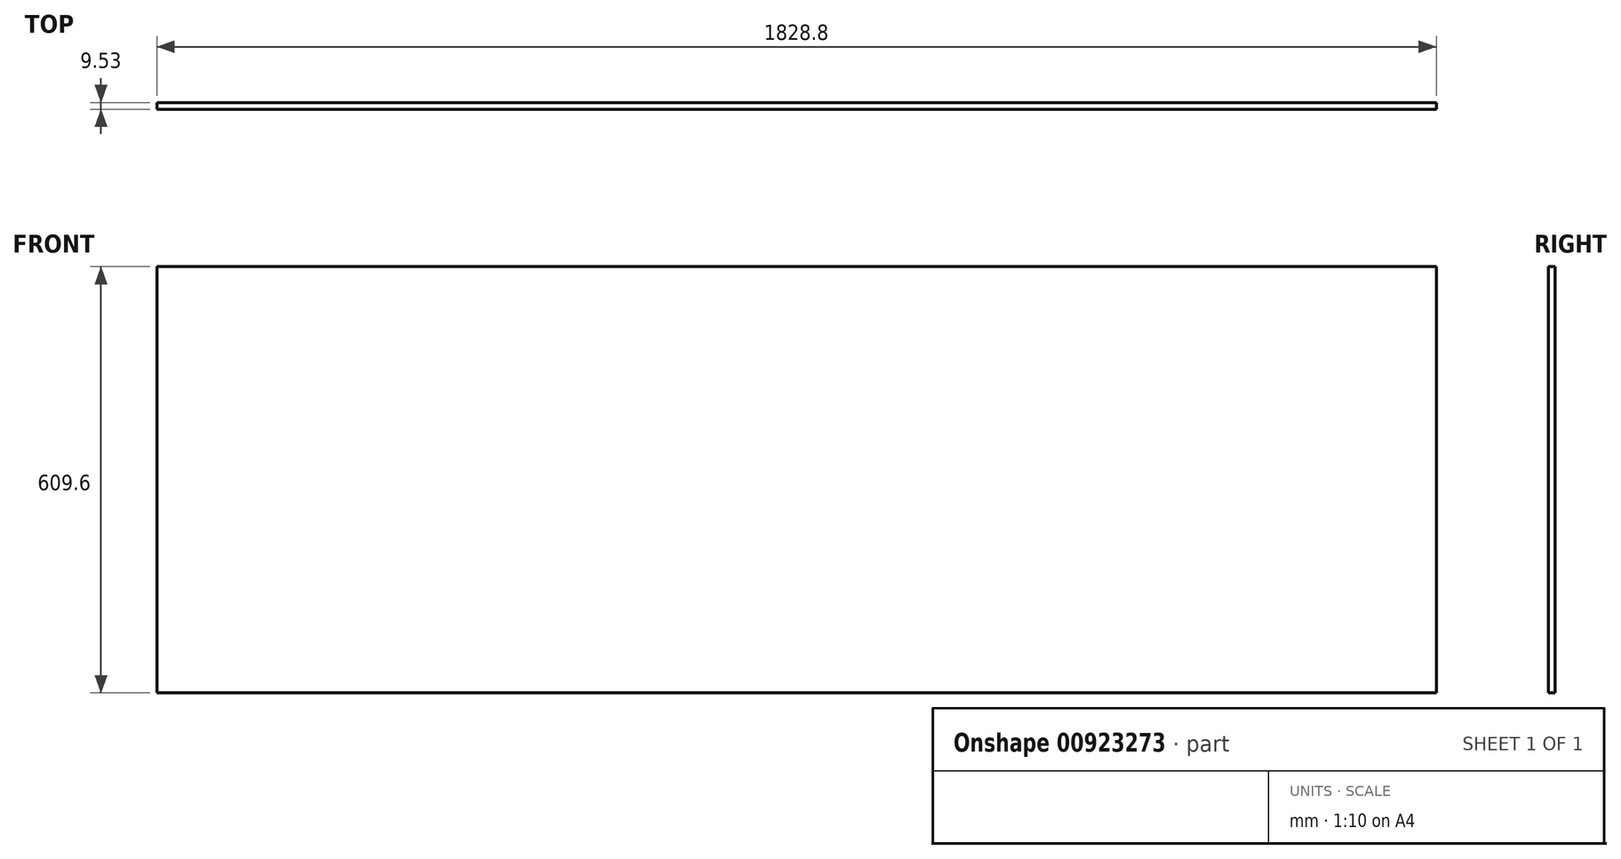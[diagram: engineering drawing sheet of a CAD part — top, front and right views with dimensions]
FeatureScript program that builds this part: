
annotation { "Feature Type Name" : "Feature", "Feature Type Description" : "" }
export const myFeature = defineFeature(function(context is Context, id is Id, definition is map)
    precondition{}
    {
        {
            var Q0;
            Q0=qCreatedBy(makeId("Front.planeOp"),FACE);
            var sketch = newSketch(context, id + "F0", { "sketchPlane" : qUnion([Q0])});
            skLineSegment(sketch, "E0.bottom", {"start": v(0, 0) * mm, "end": v(1828.8, 0) * mm});
            skLineSegment(sketch, "E0.top", {"start": v(0, 609.6) * mm, "end": v(1828.8, 609.6) * mm});
            skLineSegment(sketch, "E0.left", {"start": v(0, 0) * mm, "end": v(0, 609.6) * mm});
            skLineSegment(sketch, "E0.right", {"start": v(1828.8, 0) * mm, "end": v(1828.8, 609.6) * mm});
            skPoint(sketch, "E1", {"position": v(0, 609.6) * mm});
            skPoint(sketch, "E2", {"position": v(44.45, 609.6) * mm});
            skPoint(sketch, "E3", {"position": v(44.45, 533.4) * mm});
            skPoint(sketch, "E4", {"position": v(1784.35, 609.6) * mm});
            skPoint(sketch, "E5", {"position": v(1784.35, 533.4) * mm});
            skSolve(sketch);
        }
        {
            var Q0;
            Q0=makeQuery(id+"F0.imprint","IMPRINT",FACE,{"disambiguationData":[TD([[makeQuery(id+"F0.imprint","IMPRINT",EDGE,{"derivedFrom":sQuery(id+"F0.wireOp",EDGE,"E0.bottom")}),1.0]])]});
            extrude(context, id + "F1", {"entities" : qUnion([Q0]), "depth" : 9.52 * mm, "offsetDistance" : 25.4 * mm});
        }
    });
